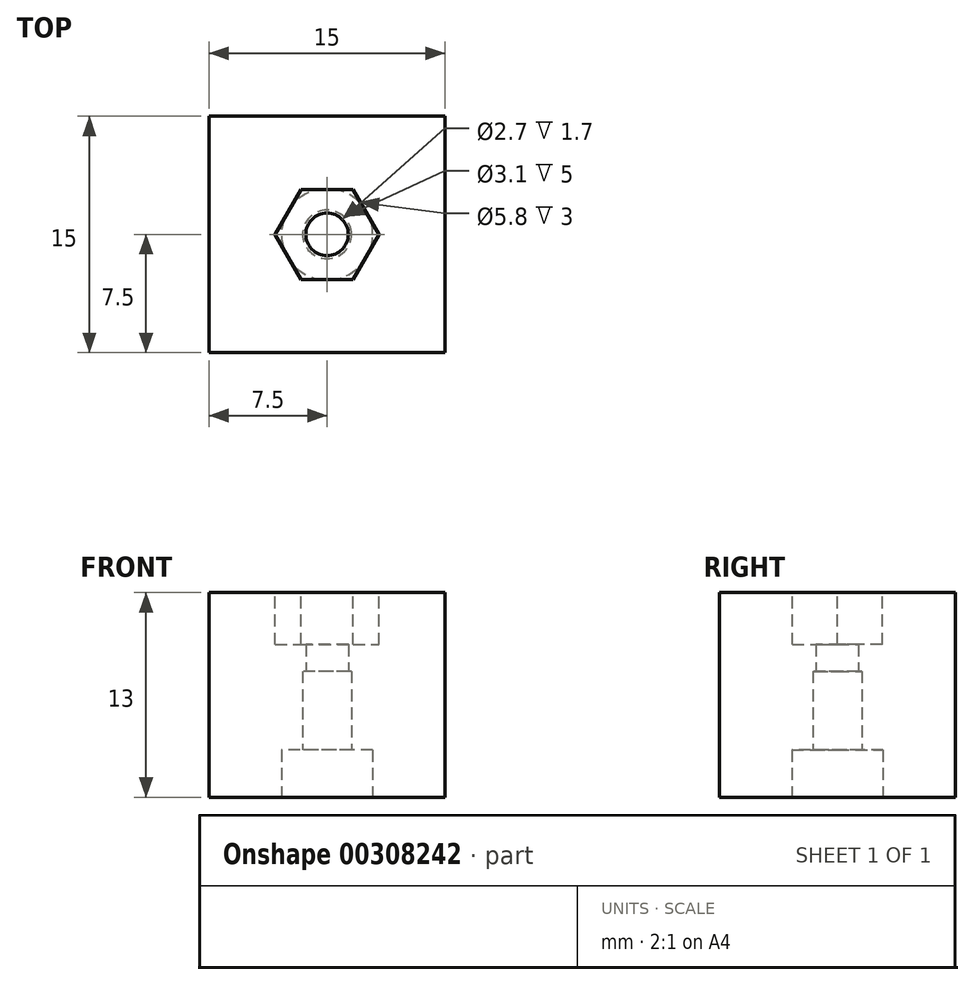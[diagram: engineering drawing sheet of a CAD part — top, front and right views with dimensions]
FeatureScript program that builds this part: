
annotation { "Feature Type Name" : "Feature", "Feature Type Description" : "" }
export const myFeature = defineFeature(function(context is Context, id is Id, definition is map)
    precondition{}
    {
        {
            var Q0;
            Q0=qCreatedBy(makeId("Top.planeOp"),FACE);
            var sketch = newSketch(context, id + "F0", { "sketchPlane" : qUnion([Q0])});
            skLineSegment(sketch, "E0.bottom", {"start": v(-7.5, 7.5) * mm, "end": v(7.5, 7.5) * mm});
            skLineSegment(sketch, "E0.top", {"start": v(-7.5, -7.5) * mm, "end": v(7.5, -7.5) * mm});
            skLineSegment(sketch, "E0.left", {"start": v(-7.5, 7.5) * mm, "end": v(-7.5, -7.5) * mm});
            skLineSegment(sketch, "E0.right", {"start": v(7.5, 7.5) * mm, "end": v(7.5, -7.5) * mm});
            skPoint(sketch, "E0.middle", {"position": v(0, 0) * mm});
            skCircle(sketch, "E1", {"center": v(0, 0) * mm, "radius": 1.35 * mm});
            skCircle(sketch, "E2", {"center": v(0, 0) * mm, "radius": 1.55 * mm});
            skCircle(sketch, "E3", {"center": v(0, 0) * mm, "radius": 2.9 * mm});
            skSolve(sketch);
        }
        {
            var Q0;
            Q0=makeQuery(id+"F0.imprint","IMPRINT",FACE,{"disambiguationData":[TD([[makeQuery(id+"F0.imprint","IMPRINT",EDGE,{"derivedFrom":sQuery(id+"F0.wireOp",EDGE,"E0.bottom")}),-1.0]])]});
            var Q1;
            Q1=makeQuery(id+"F0.imprint","IMPRINT",FACE,{"disambiguationData":[TD([[makeQuery(id+"F0.imprint","IMPRINT",EDGE,{"derivedFrom":sQuery(id+"F0.wireOp",EDGE,"E2")}),-1.0]])]});
            var Q2;
            Q2=makeQuery(id+"F0.imprint","IMPRINT",FACE,{"disambiguationData":[TD([[makeQuery(id+"F0.imprint","IMPRINT",EDGE,{"derivedFrom":sQuery(id+"F0.wireOp",EDGE,"E1")}),-1.0]])]});
            extrude(context, id + "F1", {"entities" : qUnion([Q0, Q1, Q2]), "depth" : 13 * mm, "offsetDistance" : 25 * mm});
        }
        {
            var Q0;
            Q0=makeQuery(id+"F0.imprint","IMPRINT",FACE,{"disambiguationData":[TD([[makeQuery(id+"F0.imprint","IMPRINT",EDGE,{"derivedFrom":sQuery(id+"F0.wireOp",EDGE,"E1")}),-1.0]])]});
            extrude(context, id + "F2", {"entities" : qUnion([Q0]), "operationType" : NewBodyOperationType.REMOVE, "depth" : 8 * mm, "offsetDistance" : 25 * mm});
        }
        {
            var Q0;
            Q0=makeQuery(id+"F0.imprint","IMPRINT",FACE,{"disambiguationData":[TD([[makeQuery(id+"F0.imprint","IMPRINT",EDGE,{"derivedFrom":sQuery(id+"F0.wireOp",EDGE,"E2")}),-1.0]])]});
            extrude(context, id + "F3", {"entities" : qUnion([Q0]), "operationType" : NewBodyOperationType.REMOVE, "depth" : 3 * mm, "offsetDistance" : 25 * mm});
        }
        {
            var Q0;
            Q0=makeQuery(id+"F1.opExtrude","CAP_FACE",FACE,{"disambiguationData":[OSD([sQuery(id+"F0.wireOp",EDGE,"E0.bottom"),sQuery(id+"F0.wireOp",EDGE,"E0.top"),sQuery(id+"F0.wireOp",EDGE,"E0.left"),sQuery(id+"F0.wireOp",EDGE,"E0.right"),sQuery(id+"F0.wireOp",EDGE,"E1")])],"isStart":false});
            var sketch = newSketch(context, id + "F4", { "sketchPlane" : qUnion([Q0])});
            skCircle(sketch, "E4.cCircle", {"center": v(0, 0) * mm, "radius": 3.3 * mm, "construction": true});
            skLineSegment(sketch, "E4.0", {"start": v(1.65, 2.86) * mm, "end": v(3.3, 0) * mm});
            skLineSegment(sketch, "E4.1", {"start": v(3.3, 0) * mm, "end": v(1.65, -2.86) * mm});
            skLineSegment(sketch, "E4.2", {"start": v(1.65, -2.86) * mm, "end": v(-1.65, -2.86) * mm});
            skLineSegment(sketch, "E4.3", {"start": v(-1.65, -2.86) * mm, "end": v(-3.3, 0) * mm});
            skLineSegment(sketch, "E4.4", {"start": v(-3.3, 0) * mm, "end": v(-1.65, 2.86) * mm});
            skLineSegment(sketch, "E4.5", {"start": v(-1.65, 2.86) * mm, "end": v(1.65, 2.86) * mm});
            skSolve(sketch);
        }
        {
            var Q0;
            Q0=makeQuery(id+"F4.imprint","IMPRINT",FACE,{"disambiguationData":[TD([[makeQuery(id+"F4.imprint","IMPRINT",EDGE,{"derivedFrom":sQuery(id+"F4.wireOp",EDGE,"E4.0")}),-1.0]])]});
            extrude(context, id + "F5", {"entities" : qUnion([Q0]), "operationType" : NewBodyOperationType.REMOVE, "oppositeDirection" : true, "depth" : 3.3 * mm, "offsetDistance" : 25 * mm});
        }
    });
